# Revit family: FOR UPDATE_253115_NEW
name_source: partatom
category: Plumbing Fixtures
revit_build: Autodesk Revit 2018 (Build: 20170223_1515(x64)
units: mm (PartAtom-declared; Revit-internal decimal feet)

## family parameters
Cut with Voids When Loaded = No
Host = Face
OmniClass Number = 23.31.23.00
OmniClass Title = Bidets
Part Type = Normal
Room Calculation Point = No
Round Connector Dimension = Use Diameter
Shared = No

## types (2) — shared parameters
Always visible = Yes
Connector Description = Sanitary outlet 32 mm
Default Elevation = 1219 mm
Depth = 580 mm  [stored 1.90289 ft]
Description = 1 washing area
Concealed mounting set: harmonious look, design is not disturbed by anything
Ideal for single bore faucets
Made of high-quality, long-lasting sanitary ceramic: particularly rugged, scratch-resistant material with a high degree of hardness, easy-clean and hygienic surface
Patented Durafix mounting system: concealed mounting set made of metal, particularly quick and easy to install - and completely invisible
Wall-mounted installation
With faucet deck
with overflow
Diameter = 32  [stored 0.104987 ft]
Edition number = 1
Height = 290 mm  [stored 0.951444 ft]
IFC Classification = Sanitary Terminal
Installation instructions = https://duravit-public-assets.s3.eu-central-1.amazonaws.com
Manufacturer = Duravit
Manufacturer name = DURAVIT AG
Masterformat 2014 Code = 22 41 13.19
Masterformat 2014 Description = Residential Bidets
Material 1 = Duravit - Metal - Chrome
Material main = Ceramics
Model = Architec Bidet wall mounted 253115
OmniClass Code = 23-31 23 00
OmniClass Description = Bidets
Product Guid = 5aae36d5-568e-400f-aa42-7d1c3887c786
Product SKU = architec-bidet-wall-mounted-253115
Product certification = http://pro.duravit.com
Product data url = https://bimobject.com
Product name = Architec Bidet wall mounted 253115
Product url = https://duravit-public-assets.s3.eu-central-1.amazonaws.com
QR code = https://bimobject.com
Technical description = http://pro.duravit.com
UNSPSC Code = 301815
URL = http://pro.duravit.com
Uniclass 2015 Code = Pr_40_20_06_11
Uniclass 2015 Name = Bidets
Uniformat II Code = D2030
Uniformat II Description = Sanitary Waste
Weight = 20.50 kg
Width = 365 mm  [stored 1.19751 ft]
Youtube clip = http://pro.duravit.com

## per-type parameters (varying)
| type | Material 2 |
| Architec Bidet wall mounted - 2531150000 | Duravit - Ceramic - 00 - White Alpin |
| Architec Bidet wall mounted - 25311500001 | Duravit - Ceramic - 00 - White Alpin WonderGliss |

note: [stored X ft] marks values corroborated as IEEE doubles in the binary element streams (Revit-internal decimal feet)

## geometry (parser evidence)
native form markers: Sweep x5
no freeform markers — native parametric forms only
